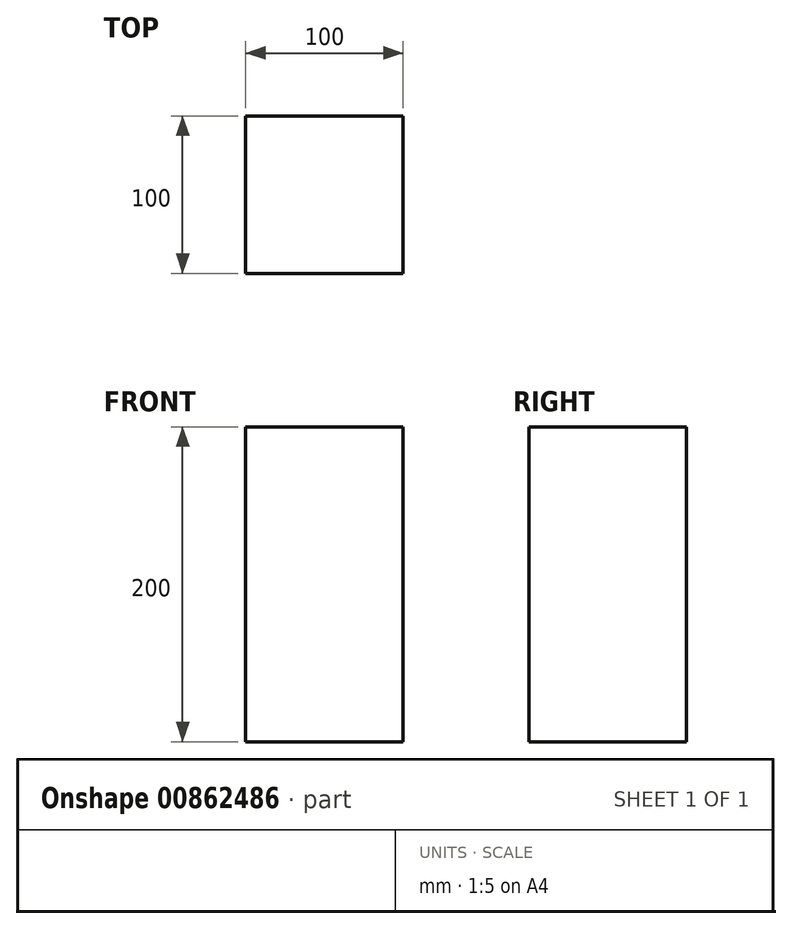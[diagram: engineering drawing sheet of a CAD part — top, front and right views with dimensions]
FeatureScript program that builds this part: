
annotation { "Feature Type Name" : "Feature", "Feature Type Description" : "" }
export const myFeature = defineFeature(function(context is Context, id is Id, definition is map)
    precondition{}
    {
        {
            var Q0;
            Q0=qCreatedBy(makeId("Top.planeOp"),FACE);
            var sketch = newSketch(context, id + "F0", { "sketchPlane" : qUnion([Q0])});
            skLineSegment(sketch, "E0.bottom", {"start": v(-50, 50) * mm, "end": v(50, 50) * mm});
            skLineSegment(sketch, "E0.top", {"start": v(-50, -50) * mm, "end": v(50, -50) * mm});
            skLineSegment(sketch, "E0.left", {"start": v(-50, 50) * mm, "end": v(-50, -50) * mm});
            skLineSegment(sketch, "E0.right", {"start": v(50, 50) * mm, "end": v(50, -50) * mm});
            skPoint(sketch, "E0.middle", {"position": v(0, 0) * mm});
            skSolve(sketch);
        }
        {
            var Q0;
            Q0=makeQuery(id+"F0.imprint","IMPRINT",FACE,{"disambiguationData":[TD([[makeQuery(id+"F0.imprint","IMPRINT",EDGE,{"derivedFrom":sQuery(id+"F0.wireOp",EDGE,"E0.bottom")}),-1.0]])]});
            extrude(context, id + "F1", {"entities" : qUnion([Q0]), "depth" : 200 * mm, "offsetDistance" : 25 * mm});
        }
    });
